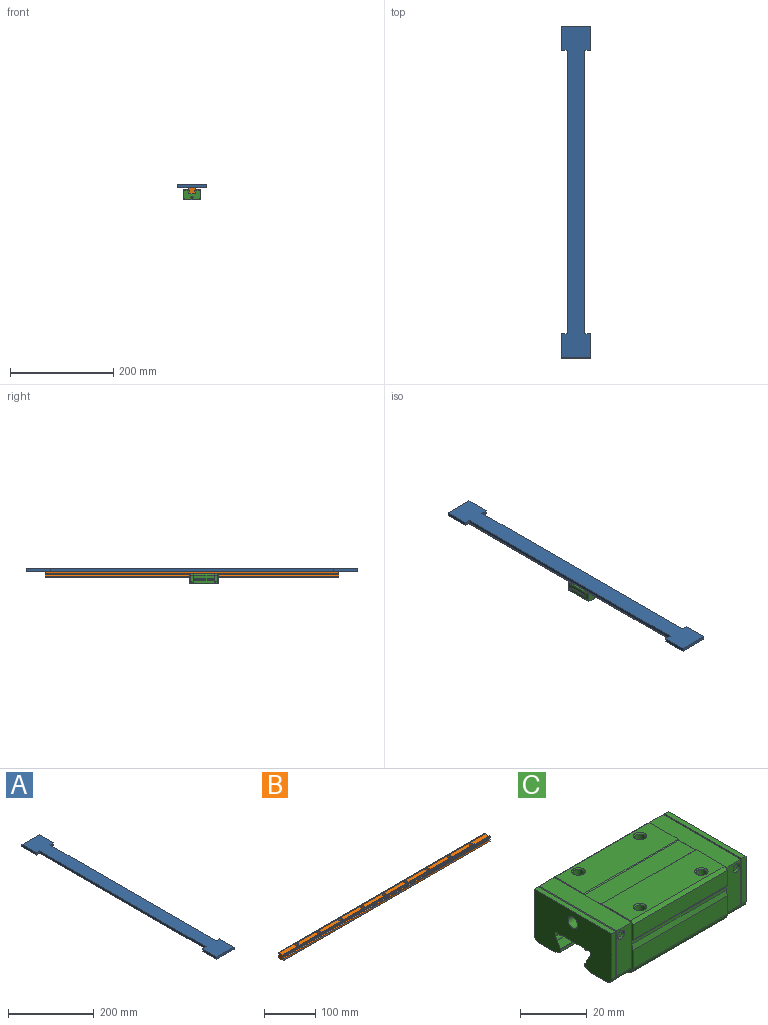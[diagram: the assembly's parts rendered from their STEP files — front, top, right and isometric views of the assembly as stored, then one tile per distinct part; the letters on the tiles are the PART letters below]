
ASSEMBLY  parts=3 mates=2
PART A: 14 faces, bbox 56.9x644x6.4 mm
  f0: plane 47x6.35mm, normal (1,0,0), area 298.4mm2, adj f3,f6,f7,f11
  f1: plane 47x6.35mm, normal (-1,0,0), area 298.4mm2, adj f3,f6,f7,f9
  f2: plane 47x6.35mm, normal (1,0,0), area 298.4mm2, adj f5,f6,f7,f12
  f3: plane 56.9x6.35mm, normal (0,1,0), area 361.3mm2, adj f0,f1,f6,f7
  f4: plane 47x6.35mm, normal (-1,0,0), area 298.4mm2, adj f5,f6,f7,f8
  f5: plane 56.9x6.35mm, normal (0,-1,0), area 361.3mm2, adj f2,f4,f6,f7
  f6: plane 644x56.9mm, normal (0,0,-1), area 24048.6mm2, adj f0,f1,f2,f3,f4,f5,f8,f9
  f7: plane 644x56.9mm, normal (0,0,1), area 24048.6mm2, adj f0,f1,f2,f3,f4,f5,f8,f9
  f8: plane 11.45x6.35mm, normal (0,1,0), area 72.7mm2, adj f4,f6,f7,f10
  f9: plane 11.45x6.35mm, normal (0,-1,0), area 72.7mm2, adj f1,f6,f7,f10
  f10: plane 550x6.35mm, normal (-1,0,0), area 3492.5mm2, adj f6,f7,f8,f9
  f11: plane 11.45x6.35mm, normal (0,-1,0), area 72.7mm2, adj f0,f6,f7,f13
  f12: plane 11.45x6.35mm, normal (0,1,0), area 72.7mm2, adj f2,f6,f7,f13
  f13: plane 550x6.35mm, normal (1,0,0), area 3492.5mm2, adj f6,f7,f11,f12
PART B: 55 faces, bbox 570x15x12.5 mm
  f0: plane 570x3.92mm, normal (0,-1,0), area 2232.7mm2, adj f1,f25,f26,f27
  f1: plane 570x0.85mm, normal (0,-0.71,-0.71), area 685.2mm2, adj f0,f2,f26,f27
  f2: plane 570x13.3mm, normal (0,0,-1), area 7437.9mm2, adj f1,f3,f26,f27,f30,f33,f36,f39
  f3: plane 570x0.85mm, normal (0,0.71,-0.71), area 685.2mm2, adj f2,f4,f26,f27
  f4: plane 570x3.92mm, normal (0,1,0), area 2232.7mm2, adj f3,f5,f26,f27
  f5: plane 570x1.85mm, normal (0,0.52,0.86), area 1234.7mm2, adj f4,f6,f26,f27
  f6: cylinder r=0.7mm len=570mm, axis (-1,0,0), area 767.8mm2, adj f5,f7,f26,f27
  f7: cylinder r=0.7mm len=570mm, axis (-1,0,0), area 190.8mm2, adj f6,f8,f26,f27
  f8: plane 570x2.43mm, normal (0,0.87,-0.5), area 1601.1mm2, adj f7,f9,f26,f27
  f9: cylinder r=1.45mm len=570mm, axis (-1,0,0), area 805.1mm2, adj f8,f10,f26,f27
  f10: plane 570x0.16mm, normal (0,0.85,-0.52), area 104.8mm2, adj f9,f11,f26,f27
  f11: plane 570x1.08mm, normal (0,1,0), area 615.6mm2, adj f10,f12,f26,f27
  f12: plane 570x0.45mm, normal (0,0.71,0.71), area 362.7mm2, adj f11,f13,f26,f27
  f13: plane 570x0.38mm, normal (0,0,1), area 218.8mm2, adj f12,f14,f26,f27
  f14: cylinder r=1.45mm len=570mm, axis (-1,0,0), area 1123.1mm2, adj f13,f15,f26,f27
  f15: plane 570x9.69mm, normal (0,0,1), area 5124.4mm2, adj f14,f16,f26,f27,f28,f31,f34,f37
  f16: cylinder r=1.45mm len=570mm, axis (-1,0,0), area 1123.1mm2, adj f15,f17,f26,f27
  f17: plane 570x0.38mm, normal (0,0,1), area 218.8mm2, adj f16,f18,f26,f27
  f18: plane 570x0.45mm, normal (0,-0.71,0.71), area 362.7mm2, adj f17,f19,f26,f27
  f19: plane 570x1.08mm, normal (0,-1,0), area 615.6mm2, adj f18,f20,f26,f27
  f20: plane 570x0.16mm, normal (0,-0.85,-0.52), area 104.8mm2, adj f19,f21,f26,f27
  f21: cylinder r=1.45mm len=570mm, axis (-1,0,0), area 805.1mm2, adj f20,f22,f26,f27
  f22: plane 570x2.43mm, normal (0,-0.87,-0.5), area 1601.1mm2, adj f21,f23,f26,f27
  f23: cylinder r=0.7mm len=570mm, axis (-1,0,0), area 190.8mm2, adj f22,f24,f26,f27
  f24: cylinder r=0.7mm len=570mm, axis (-1,0,0), area 767.8mm2, adj f23,f25,f26,f27
  f25: plane 570x1.85mm, normal (0,-0.52,0.86), area 1234.7mm2, adj f0,f24,f26,f27
  f26: plane 15x12.5mm, normal (1,0,0), area 168.5mm2, adj f0,f1,f2,f3,f4,f5,f6,f7
  f27: plane 15x12.5mm, normal (-1,0,0), area 168.5mm2, adj f0,f1,f2,f3,f4,f5,f6,f7
  f28: cylinder r=3.75mm len=7.5mm, axis (0,0,-1), area 124.9mm2, adj f15,f29
  f29: plane 7.5x7.5mm, normal (0,0,1), area 28.3mm2, adj f28,f30
  f30: cylinder r=2.25mm len=7.2mm, axis (0,0,-1), area 101.8mm2, adj f2,f29
  f31: cylinder r=3.75mm len=7.5mm, axis (0,0,-1), area 124.9mm2, adj f15,f32
  f32: plane 7.5x7.5mm, normal (0,0,1), area 28.3mm2, adj f31,f33
  f33: cylinder r=2.25mm len=7.2mm, axis (0,0,-1), area 101.8mm2, adj f2,f32
  f34: cylinder r=3.75mm len=7.5mm, axis (0,0,-1), area 124.9mm2, adj f15,f35
  f35: plane 7.5x7.5mm, normal (0,0,1), area 28.3mm2, adj f34,f36
  f36: cylinder r=2.25mm len=7.2mm, axis (0,0,-1), area 101.8mm2, adj f2,f35
  f37: cylinder r=3.75mm len=7.5mm, axis (0,0,-1), area 124.9mm2, adj f15,f38
  f38: plane 7.5x7.5mm, normal (0,0,1), area 28.3mm2, adj f37,f39
  f39: cylinder r=2.25mm len=7.2mm, axis (0,0,-1), area 101.8mm2, adj f2,f38
  f40: cylinder r=3.75mm len=7.5mm, axis (0,0,-1), area 124.9mm2, adj f15,f41
  f41: plane 7.5x7.5mm, normal (0,0,1), area 28.3mm2, adj f40,f42
  f42: cylinder r=2.25mm len=7.2mm, axis (0,0,-1), area 101.8mm2, adj f2,f41
  f43: cylinder r=3.75mm len=7.5mm, axis (0,0,-1), area 124.9mm2, adj f15,f44
  f44: plane 7.5x7.5mm, normal (0,0,1), area 28.3mm2, adj f43,f45
  f45: cylinder r=2.25mm len=7.2mm, axis (0,0,-1), area 101.8mm2, adj f2,f44
  f46: cylinder r=3.75mm len=7.5mm, axis (0,0,-1), area 124.9mm2, adj f15,f47
  f47: plane 7.5x7.5mm, normal (0,0,1), area 28.3mm2, adj f46,f48
  f48: cylinder r=2.25mm len=7.2mm, axis (0,0,-1), area 101.8mm2, adj f2,f47
  f49: cylinder r=3.75mm len=7.5mm, axis (0,0,-1), area 124.9mm2, adj f15,f50
  f50: plane 7.5x7.5mm, normal (0,0,1), area 28.3mm2, adj f49,f51
  f51: cylinder r=2.25mm len=7.2mm, axis (0,0,-1), area 101.8mm2, adj f2,f50
  f52: cylinder r=3.75mm len=7.5mm, axis (0,0,-1), area 124.9mm2, adj f15,f53
  f53: plane 7.5x7.5mm, normal (0,0,1), area 28.3mm2, adj f52,f54
  f54: cylinder r=2.25mm len=7.2mm, axis (0,0,-1), area 101.8mm2, adj f2,f53
PART C: 100 faces, bbox 56.9x34x19.5 mm
  f0: plane 16.6x6.3mm, normal (0,-1,0), area 97.5mm2, adj f4,f15,f24,f76,f98
  f1: plane 16.6x1.7mm, normal (0,-1,0), area 28.2mm2, adj f4,f25,f31,f73
  f2: plane 16.6x6.3mm, normal (0,1,0), area 97.5mm2, adj f5,f15,f24,f80,f99
  f3: plane 16.6x1.7mm, normal (0,1,0), area 28.2mm2, adj f5,f25,f31,f73
  f4: cylinder r=2mm len=8.5mm, axis (1,0,0), area 26.2mm2, adj f0,f1,f15,f30,f31,f73,f98
  f5: cylinder r=2mm len=8.5mm, axis (1,0,0), area 26.2mm2, adj f2,f3,f15,f29,f31,f73,f99
  f6: plane 32.8x0.5mm, normal (0.71,0,0.71), area 22.8mm2, adj f24,f73,f98,f99
  f7: plane 16.6x6.3mm, normal (0,-1,0), area 97.5mm2, adj f11,f14,f27,f74,f97
  f8: plane 16.6x1.7mm, normal (0,-1,0), area 28.2mm2, adj f11,f26,f28,f72
  f9: plane 16.6x1.7mm, normal (0,1,0), area 28.2mm2, adj f12,f26,f28,f72
  f10: plane 16.6x6.3mm, normal (0,1,0), area 97.5mm2, adj f12,f14,f27,f78,f96
  f11: cylinder r=2mm len=8.5mm, axis (-1,0,0), area 26.2mm2, adj f7,f8,f14,f28,f30,f72,f97
  f12: cylinder r=2mm len=8.5mm, axis (-1,0,0), area 26.2mm2, adj f9,f10,f14,f28,f29,f72,f96
  f13: plane 32.8x0.5mm, normal (-0.71,0,0.71), area 22.8mm2, adj f27,f72,f96,f97
  f14: plane 34x19.5mm, normal (-1,0,0), area 38.1mm2, adj f7,f10,f11,f12,f16,f17,f20,f21
  f15: plane 34x19.5mm, normal (1,0,0), area 38.1mm2, adj f0,f2,f4,f5,f16,f17,f20,f21
  f16: plane 39.9x5.95mm, normal (0,0,-1), area 237.2mm2, adj f14,f15,f33,f94
  f17: plane 39.9x5.95mm, normal (0,0,-1), area 237.2mm2, adj f14,f15,f34,f95
  f18: plane 56.9x1.47mm, normal (0,-0.52,-0.86), area 97.6mm2, adj f28,f29,f31,f53
  f19: plane 56.9x1.47mm, normal (0,0.52,-0.86), area 97.6mm2, adj f28,f30,f31,f71
  f20: plane 39.9x6.69mm, normal (0,-1,0), area 266.9mm2, adj f14,f15,f33,f92
  f21: plane 39.9x5.52mm, normal (0,-1,0), area 220.2mm2, adj f14,f15,f32,f93
  f22: plane 39.9x6.69mm, normal (0,1,0), area 266.9mm2, adj f14,f15,f34,f88
  f23: plane 39.9x5.52mm, normal (0,1,0), area 220.2mm2, adj f14,f15,f35,f89
  f24: plane 32.8x6.3mm, normal (0,0,1), area 206.6mm2, adj f0,f2,f6,f15
  f25: plane 32.8x1.7mm, normal (0,0,1), area 55.8mm2, adj f1,f3,f31,f73
  f26: plane 32.8x1.7mm, normal (0,0,1), area 55.8mm2, adj f8,f9,f28,f72
  f27: plane 32.8x6.3mm, normal (0,0,1), area 206.6mm2, adj f7,f10,f13,f14
  f28: plane 32.8x18.6mm, normal (-1,0,0), area 501.5mm2, adj f8,f9,f11,f12,f18,f19,f26,f29
  f29: plane 56.9x7.29mm, normal (0,0,-1), area 146.6mm2, adj f5,f12,f14,f15,f18,f28,f31,f95
  f30: plane 56.9x7.29mm, normal (0,0,-1), area 146.6mm2, adj f4,f11,f14,f15,f19,f28,f31,f94
  f31: plane 32.8x18.6mm, normal (1,0,0), area 501.5mm2, adj f1,f3,f4,f5,f18,f19,f25,f29
  f32: plane 39.9x0.98mm, normal (0,-0.71,0.71), area 55.3mm2, adj f14,f15,f21,f40
  f33: cylinder r=2.5mm len=39.9mm, axis (-1,0,0), area 156.7mm2, adj f14,f15,f16,f20
  f34: cylinder r=2.5mm len=39.9mm, axis (-1,0,0), area 156.7mm2, adj f14,f15,f17,f22
  f35: plane 39.9x0.98mm, normal (0,0.71,0.71), area 55.3mm2, adj f14,f15,f23,f36
  f36: plane 39.9x12.22mm, normal (0,0,1), area 462.4mm2, adj f14,f15,f35,f37,f47,f50
  f37: plane 39.9x0.3mm, normal (0,-0.71,0.71), area 16.9mm2, adj f14,f15,f36,f38
  f38: plane 39.9x7mm, normal (0,0,1), area 279.3mm2, adj f14,f15,f37,f39
  f39: plane 39.9x0.3mm, normal (0,0.71,0.71), area 16.9mm2, adj f14,f15,f38,f40
  f40: plane 39.9x12.22mm, normal (0,0,1), area 462.4mm2, adj f14,f15,f32,f39,f41,f44
  f41: cone r=2mm half-angle=45deg, axis (0,0,1), area 6.1mm2, adj f40,f42
  f42: cylinder r=1.62mm len=8.02mm, axis (0,0,-1), area 81.7mm2, adj f41,f43
  f43: cone r=1.62mm half-angle=60deg, axis (0,0,1), area 9.5mm2, adj f42
  f44: cone r=2mm half-angle=45deg, axis (0,0,1), area 6.1mm2, adj f40,f45
  f45: cylinder r=1.62mm len=8.02mm, axis (0,0,-1), area 81.7mm2, adj f44,f46
  f46: cone r=1.62mm half-angle=60deg, axis (0,0,1), area 9.5mm2, adj f45
  f47: cone r=2mm half-angle=45deg, axis (0,0,1), area 6.1mm2, adj f36,f48
  f48: cylinder r=1.62mm len=8.02mm, axis (0,0,-1), area 81.7mm2, adj f47,f49
  f49: cone r=1.62mm half-angle=60deg, axis (0,0,1), area 9.5mm2, adj f48
  f50: cone r=2mm half-angle=45deg, axis (0,0,1), area 6.1mm2, adj f36,f51
  f51: cylinder r=1.62mm len=8.02mm, axis (0,0,-1), area 81.7mm2, adj f50,f52
  f52: cone r=1.62mm half-angle=60deg, axis (0,0,1), area 9.5mm2, adj f51
  f53: cylinder r=0.7mm len=56.9mm, axis (-1,0,0), area 76.6mm2, adj f18,f28,f31,f54
  f54: cylinder r=0.7mm len=56.9mm, axis (-1,0,0), area 19mm2, adj f28,f31,f53,f55
  f55: plane 56.9x2.43mm, normal (0,-0.87,0.5), area 159.8mm2, adj f28,f31,f54,f56
  f56: cylinder r=1.45mm len=56.9mm, axis (-1,0,0), area 80.4mm2, adj f28,f31,f55,f57
  f57: plane 56.9x0.16mm, normal (0,-0.85,0.52), area 10.5mm2, adj f28,f31,f56,f58
  f58: plane 56.9x1.08mm, normal (0,-1,0), area 61.5mm2, adj f28,f31,f57,f59
  f59: plane 56.9x0.45mm, normal (0,-0.71,-0.71), area 36.2mm2, adj f28,f31,f58,f60
  f60: plane 56.9x0.38mm, normal (0,0,-1), area 21.8mm2, adj f28,f31,f59,f61
  f61: cylinder r=1.45mm len=56.9mm, axis (-1,0,0), area 112.1mm2, adj f28,f31,f60,f62
  f62: plane 56.9x9.69mm, normal (0,0,-1), area 551.2mm2, adj f28,f31,f61,f63
  f63: cylinder r=1.45mm len=56.9mm, axis (-1,0,0), area 112.1mm2, adj f28,f31,f62,f64
  f64: plane 56.9x0.38mm, normal (0,0,-1), area 21.8mm2, adj f28,f31,f63,f65
  f65: plane 56.9x0.45mm, normal (0,0.71,-0.71), area 36.2mm2, adj f28,f31,f64,f66
  f66: plane 56.9x1.08mm, normal (0,1,0), area 61.5mm2, adj f28,f31,f65,f67
  f67: plane 56.9x0.16mm, normal (0,0.85,0.52), area 10.5mm2, adj f28,f31,f66,f68
  f68: cylinder r=1.45mm len=56.9mm, axis (-1,0,0), area 80.4mm2, adj f28,f31,f67,f69
  f69: plane 56.9x2.43mm, normal (0,0.87,0.5), area 159.8mm2, adj f28,f31,f68,f70
  f70: cylinder r=0.7mm len=56.9mm, axis (-1,0,0), area 19mm2, adj f28,f31,f69,f71
  f71: cylinder r=0.7mm len=56.9mm, axis (-1,0,0), area 76.6mm2, adj f19,f28,f31,f70
  f72: plane 32.8x17.92mm, normal (1,0,0), area 33.4mm2, adj f8,f9,f11,f12,f13,f26,f96,f97
  f73: plane 32.8x17.92mm, normal (-1,0,0), area 33.4mm2, adj f1,f3,f4,f5,f6,f25,f98,f99
  f74: cylinder r=1.5mm len=3mm, axis (0,-1,0), area 9.4mm2, adj f7,f75
  f75: plane 3x3mm, normal (0,-1,0), area 7.1mm2, adj f74
  f76: cylinder r=1.5mm len=3mm, axis (0,-1,0), area 9.4mm2, adj f0,f77
  f77: plane 3x3mm, normal (0,-1,0), area 7.1mm2, adj f76
  f78: cylinder r=1.5mm len=3mm, axis (0,1,0), area 9.4mm2, adj f10,f79
  f79: plane 3x3mm, normal (0,1,0), area 7.1mm2, adj f78
  f80: cylinder r=1.5mm len=3mm, axis (0,1,0), area 9.4mm2, adj f2,f81
  f81: plane 3x3mm, normal (0,1,0), area 7.1mm2, adj f80
  f82: cylinder r=2mm len=4.5mm, axis (1,0,0), area 56.5mm2, adj f28,f83
  f83: plane 4x4mm, normal (-1,0,0), area 12.6mm2, adj f82
  f84: plane 4x4mm, normal (1,0,0), area 12.6mm2, adj f85
  f85: cylinder r=2mm len=4.5mm, axis (1,0,0), area 56.5mm2, adj f31,f84
  f86: plane 39.9x1.13mm, normal (0,1,0), area 45.2mm2, adj f14,f15,f87,f88
  f87: cylinder r=0.5mm len=39.9mm, axis (-1,0,0), area 12.2mm2, adj f14,f15,f86,f89
  f88: plane 39.9x1.81mm, normal (0,0.96,0.27), area 74.9mm2, adj f14,f15,f22,f86
  f89: plane 39.9x0.58mm, normal (0,0.82,-0.58), area 28.3mm2, adj f14,f15,f23,f87
  f90: plane 39.9x1.13mm, normal (0,-1,0), area 45.2mm2, adj f14,f15,f91,f92
  f91: cylinder r=0.5mm len=39.9mm, axis (-1,0,0), area 12.2mm2, adj f14,f15,f90,f93
  f92: plane 39.9x1.81mm, normal (0,-0.96,0.27), area 74.9mm2, adj f14,f15,f20,f90
  f93: plane 39.9x0.58mm, normal (0,-0.82,-0.58), area 28.3mm2, adj f14,f15,f21,f91
  f94: plane 39.9x0.87mm, normal (0,0.5,-0.87), area 40mm2, adj f14,f15,f16,f30
  f95: plane 39.9x0.87mm, normal (0,-0.5,-0.87), area 40mm2, adj f14,f15,f17,f29
  f96: plane 17.92x0.5mm, normal (-0.71,0.71,0), area 12.2mm2, adj f10,f12,f13,f72
  f97: plane 17.92x0.5mm, normal (-0.71,-0.71,0), area 12.2mm2, adj f7,f11,f13,f72
  f98: plane 17.92x0.5mm, normal (0.71,-0.71,0), area 12.2mm2, adj f0,f4,f6,f73
  f99: plane 17.92x0.5mm, normal (0.71,0.71,0), area 12.2mm2, adj f2,f5,f6,f73
PLACE A t=(-9.16,-2.97,-7.89)mm fixed
PLACE B rot(axis=(0.71,-0.71,0),180deg) t=(-9.16,657.03,-14.24)mm
PLACE C rot(axis=(0.71,0.71,0),180deg) t=(-9.16,-26.11,-18.74)mm
MATE slider C.f61 <-> B.f16  axis (0,-1,0) through (-3.41,-54.56,-27.87)mm
MATE fastened B.f40 <-> A.f6  axis (0,0,1) through (-9.16,-2.97,-14.24)mm
